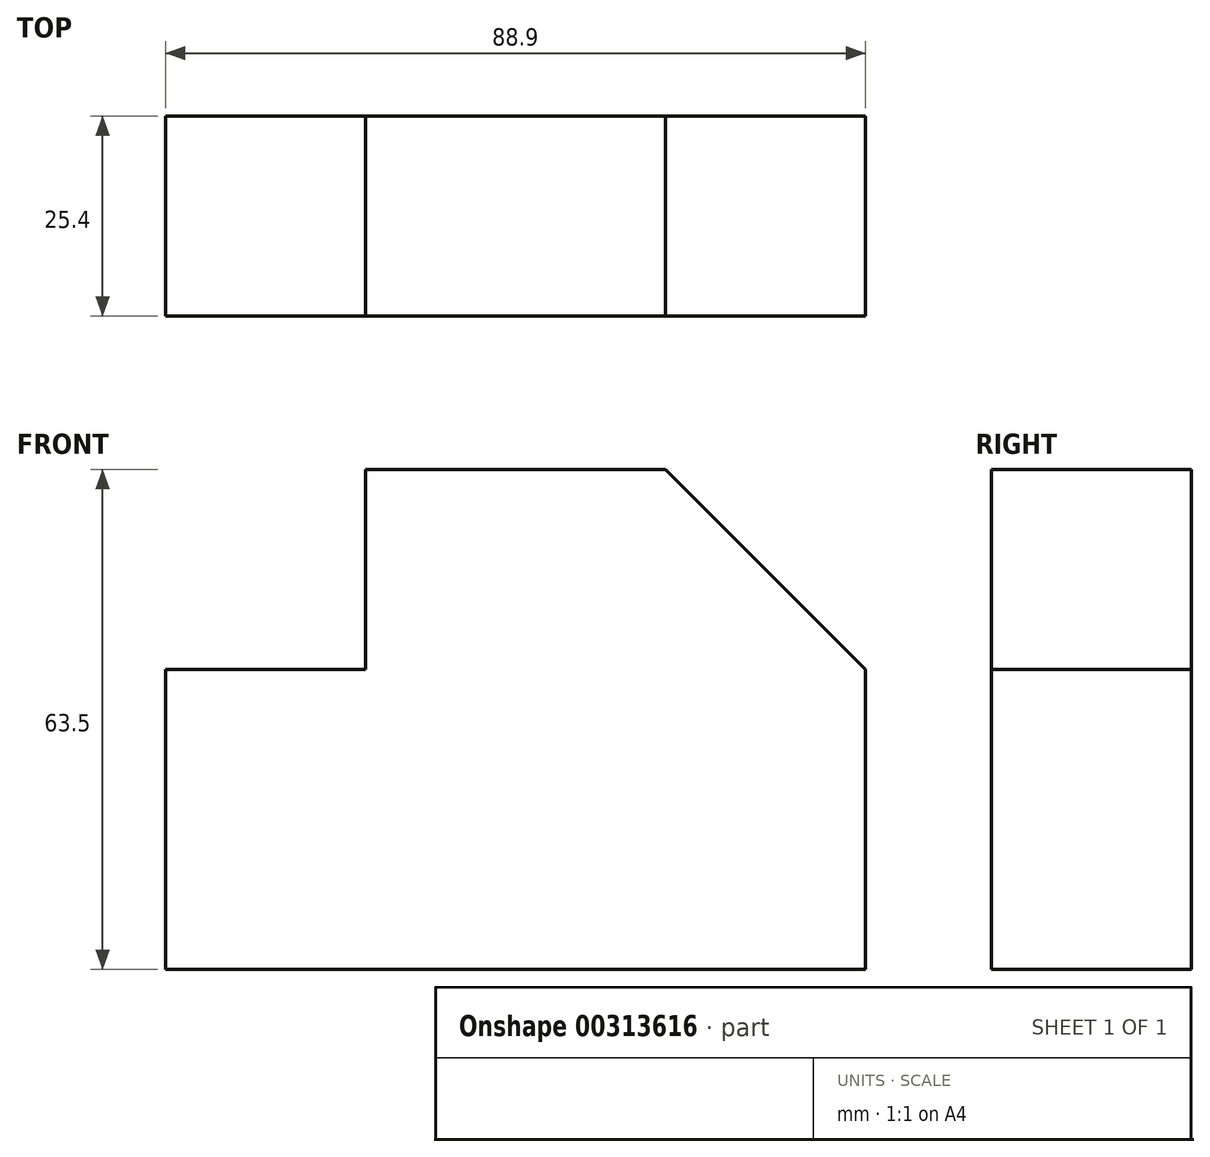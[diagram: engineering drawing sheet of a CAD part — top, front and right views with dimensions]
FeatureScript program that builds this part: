
annotation { "Feature Type Name" : "Feature", "Feature Type Description" : "" }
export const myFeature = defineFeature(function(context is Context, id is Id, definition is map)
    precondition{}
    {
        {
            var Q0;
            Q0=qCreatedBy(makeId("Front.planeOp"),FACE);
            var sketch = newSketch(context, id + "F0", { "sketchPlane" : qUnion([Q0])});
            skLineSegment(sketch, "E0", {"start": v(-46.46, -35.13) * mm, "end": v(42.44, -35.13) * mm});
            skLineSegment(sketch, "E1", {"start": v(42.44, -35.13) * mm, "end": v(42.44, 2.97) * mm});
            skLineSegment(sketch, "E2", {"start": v(-46.46, -35.13) * mm, "end": v(-46.46, 2.97) * mm});
            skLineSegment(sketch, "E3", {"start": v(-46.46, 2.97) * mm, "end": v(-21.06, 2.97) * mm});
            skLineSegment(sketch, "E4", {"start": v(-21.06, 2.97) * mm, "end": v(-21.06, 28.37) * mm});
            skLineSegment(sketch, "E5", {"start": v(-21.06, 28.37) * mm, "end": v(17.04, 28.37) * mm});
            skLineSegment(sketch, "E6", {"start": v(17.04, 28.37) * mm, "end": v(42.44, 2.97) * mm});
            skSolve(sketch);
        }
        {
            var Q0;
            Q0=makeQuery(id+"F0.imprint","IMPRINT",FACE,{"disambiguationData":[TD([[makeQuery(id+"F0.imprint","IMPRINT",EDGE,{"derivedFrom":sQuery(id+"F0.wireOp",EDGE,"E0")}),1.0]])]});
            extrude(context, id + "F1", {"entities" : qUnion([Q0]), "oppositeDirection" : true, "depth" : 25.4 * mm});
        }
    });
